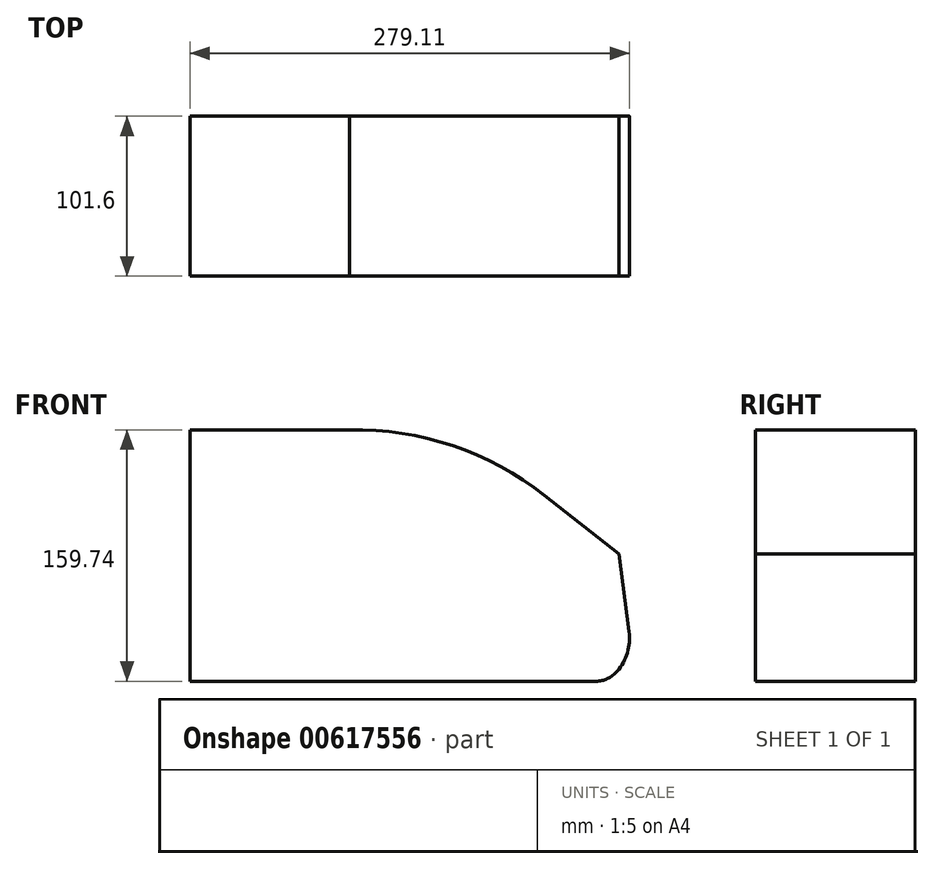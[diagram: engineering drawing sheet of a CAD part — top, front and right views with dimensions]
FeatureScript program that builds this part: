
annotation { "Feature Type Name" : "Feature", "Feature Type Description" : "" }
export const myFeature = defineFeature(function(context is Context, id is Id, definition is map)
    precondition{}
    {
        {
            var Q0;
            Q0=qCreatedBy(makeId("Front.planeOp"),FACE);
            var sketch = newSketch(context, id + "F0", { "sketchPlane" : qUnion([Q0])});
            skLineSegment(sketch, "E0", {"start": v(0, 0) * mm, "end": v(149.21, 0) * mm});
            skLineSegment(sketch, "E1", {"start": v(149.21, 0) * mm, "end": v(257.68, 0) * mm});
            skArc(sketch, "E2", {"start": v(257.68, 0) * mm, "mid": v(265.17, 1.64) * mm, "end": v(271.28, 6.26) * mm});
            skArc(sketch, "E3", {"start": v(271.28, 6.26) * mm, "mid": v(277.75, 18.12) * mm, "end": v(278.84, 31.59) * mm});
            skLineSegment(sketch, "E4", {"start": v(278.84, 31.59) * mm, "end": v(272.5, 80.96) * mm});
            skLineSegment(sketch, "E5", {"start": v(272.5, 80.96) * mm, "end": v(225.18, 118.13) * mm});
            skArc(sketch, "E6", {"start": v(225.18, 118.13) * mm, "mid": v(166.79, 149.62) * mm, "end": v(101.22, 159.7) * mm});
            skLineSegment(sketch, "E7", {"start": v(101.22, 159.7) * mm, "end": v(0, 159.7) * mm});
            skLineSegment(sketch, "E8", {"start": v(0, 159.7) * mm, "end": v(0, 0) * mm});
            skSolve(sketch);
        }
        {
            var Q0;
            Q0 = qSketchRegion(id + "F0", true);
            extrude(context, id + "F1", {"entities" : qUnion([Q0]), "depth" : 50.8 * mm, "offsetDistance" : 25.4 * mm});
        }
        {
            var Q0;
            Q0=makeQuery(id+"F1.opExtrude","CAP_FACE",FACE,{"disambiguationData":[OSD([sQuery(id+"F0.wireOp",EDGE,"E0"),sQuery(id+"F0.wireOp",EDGE,"E1"),sQuery(id+"F0.wireOp",EDGE,"E2"),sQuery(id+"F0.wireOp",EDGE,"E3"),sQuery(id+"F0.wireOp",EDGE,"E4"),sQuery(id+"F0.wireOp",EDGE,"E5"),sQuery(id+"F0.wireOp",EDGE,"E6"),sQuery(id+"F0.wireOp",EDGE,"E7"),sQuery(id+"F0.wireOp",EDGE,"E8")])],"isStart":false});
            var sketch = newSketch(context, id + "F2", { "sketchPlane" : qUnion([Q0])});
            skSolve(sketch);
        }
        {
            var Q0;
            Q0=makeQuery(id+"F1.opExtrude","CAP_FACE",FACE,{"disambiguationData":[OSD([sQuery(id+"F0.wireOp",EDGE,"E0"),sQuery(id+"F0.wireOp",EDGE,"E1"),sQuery(id+"F0.wireOp",EDGE,"E2"),sQuery(id+"F0.wireOp",EDGE,"E3"),sQuery(id+"F0.wireOp",EDGE,"E4"),sQuery(id+"F0.wireOp",EDGE,"E5"),sQuery(id+"F0.wireOp",EDGE,"E6"),sQuery(id+"F0.wireOp",EDGE,"E7"),sQuery(id+"F0.wireOp",EDGE,"E8")])],"isStart":true});
            var Q1;
            Q1 = qSketchRegion(id + "F2", true);
            var Q2;
            Q2=makeQuery(id+"F2.imprint","IMPRINT",FACE,{"disambiguationData":[TD([[makeQuery(id+"F2.imprint","IMPRINT",EDGE,{"derivedFrom":makeQuery(id+"F1.opExtrude","CAP_EDGE",EDGE,{"disambiguationData":[OSD([sQuery(id+"F0.wireOp",EDGE,"E2")])],"isStart":false})}),1.0]])]});
            extrude(context, id + "F3", {"entities" : qUnion([Q0, Q1, Q2]), "operationType" : NewBodyOperationType.ADD, "depth" : 50.8 * mm, "offsetDistance" : 25.4 * mm});
        }
    });
